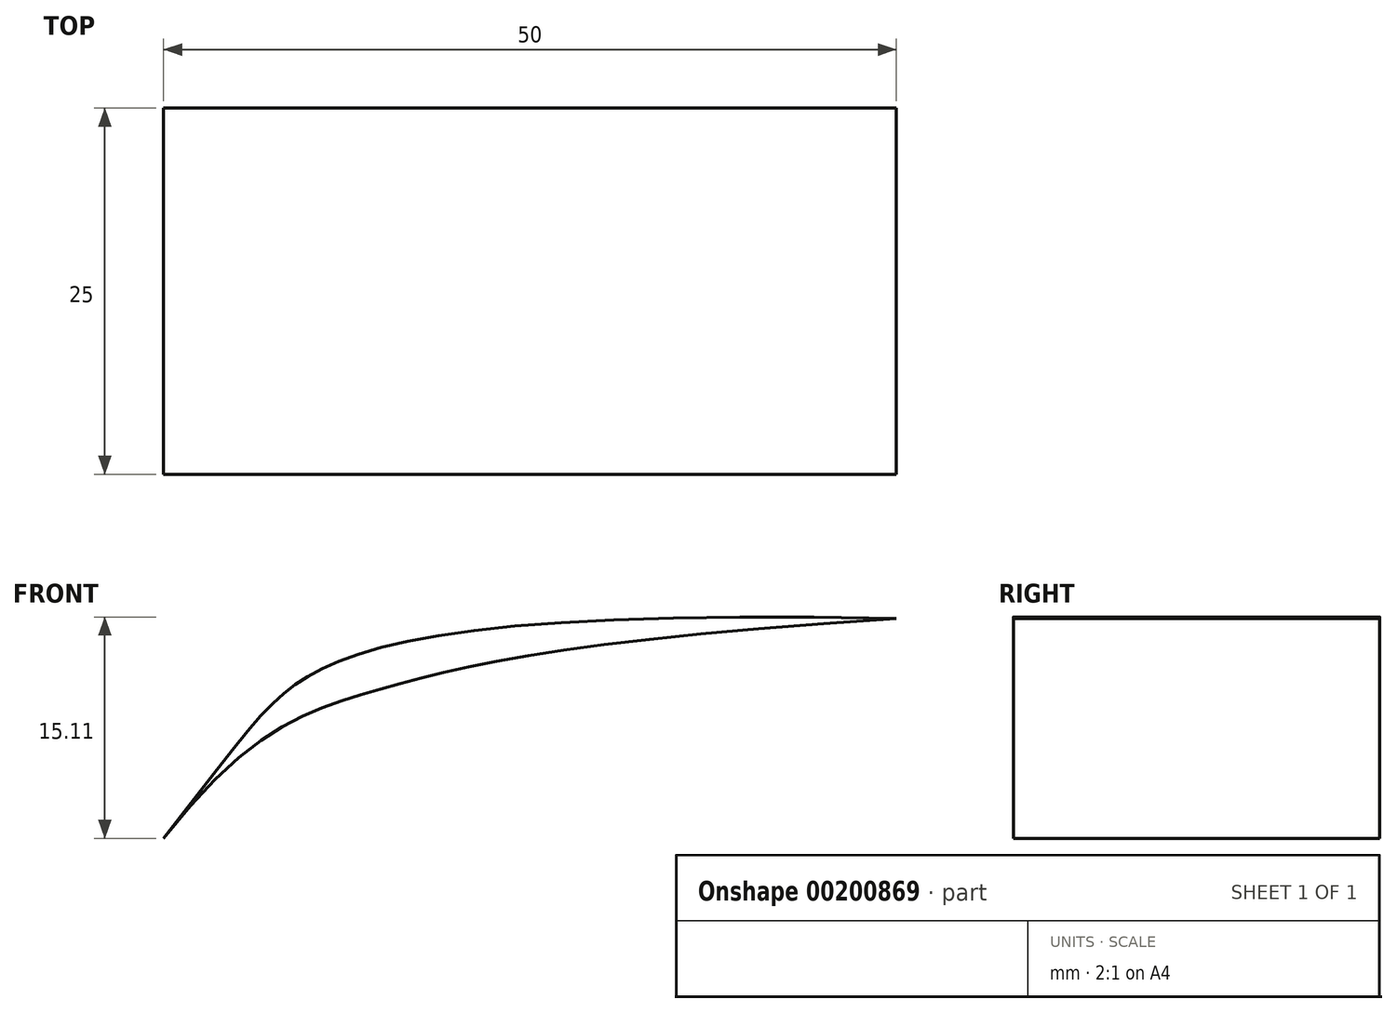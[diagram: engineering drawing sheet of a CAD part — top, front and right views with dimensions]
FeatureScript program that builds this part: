
annotation { "Feature Type Name" : "Feature", "Feature Type Description" : "" }
export const myFeature = defineFeature(function(context is Context, id is Id, definition is map)
    precondition{}
    {
        {
            var Q0;
            Q0=qCreatedBy(makeId("Front.planeOp"),FACE);
            var sketch = newSketch(context, id + "F0", { "sketchPlane" : qUnion([Q0])});
            skFitSpline(sketch, "E0", {"points": [v(-21.6, -7.55) * mm, v(-12.15, 3.25) * mm, v(28.4, 7.45) * mm], "startDerivative": vector(47.3, 60.83) * mm, "endDerivative": vector(135.73, -3.08) * mm});
            skFitSpline(sketch, "E1", {"points": [v(-21.6, -7.55) * mm, v(-7.68, 2.37) * mm, v(28.4, 7.45) * mm], "startDerivative": vector(43.33, 55.72) * mm, "endDerivative": vector(120.28, 7.83) * mm});
            skSolve(sketch);
        }
        {
            var Q0;
            Q0 = qSketchRegion(id + "F0", true);
            extrude(context, id + "F1", {"entities" : qUnion([Q0]), "depth" : 25 * mm});
        }
    });
